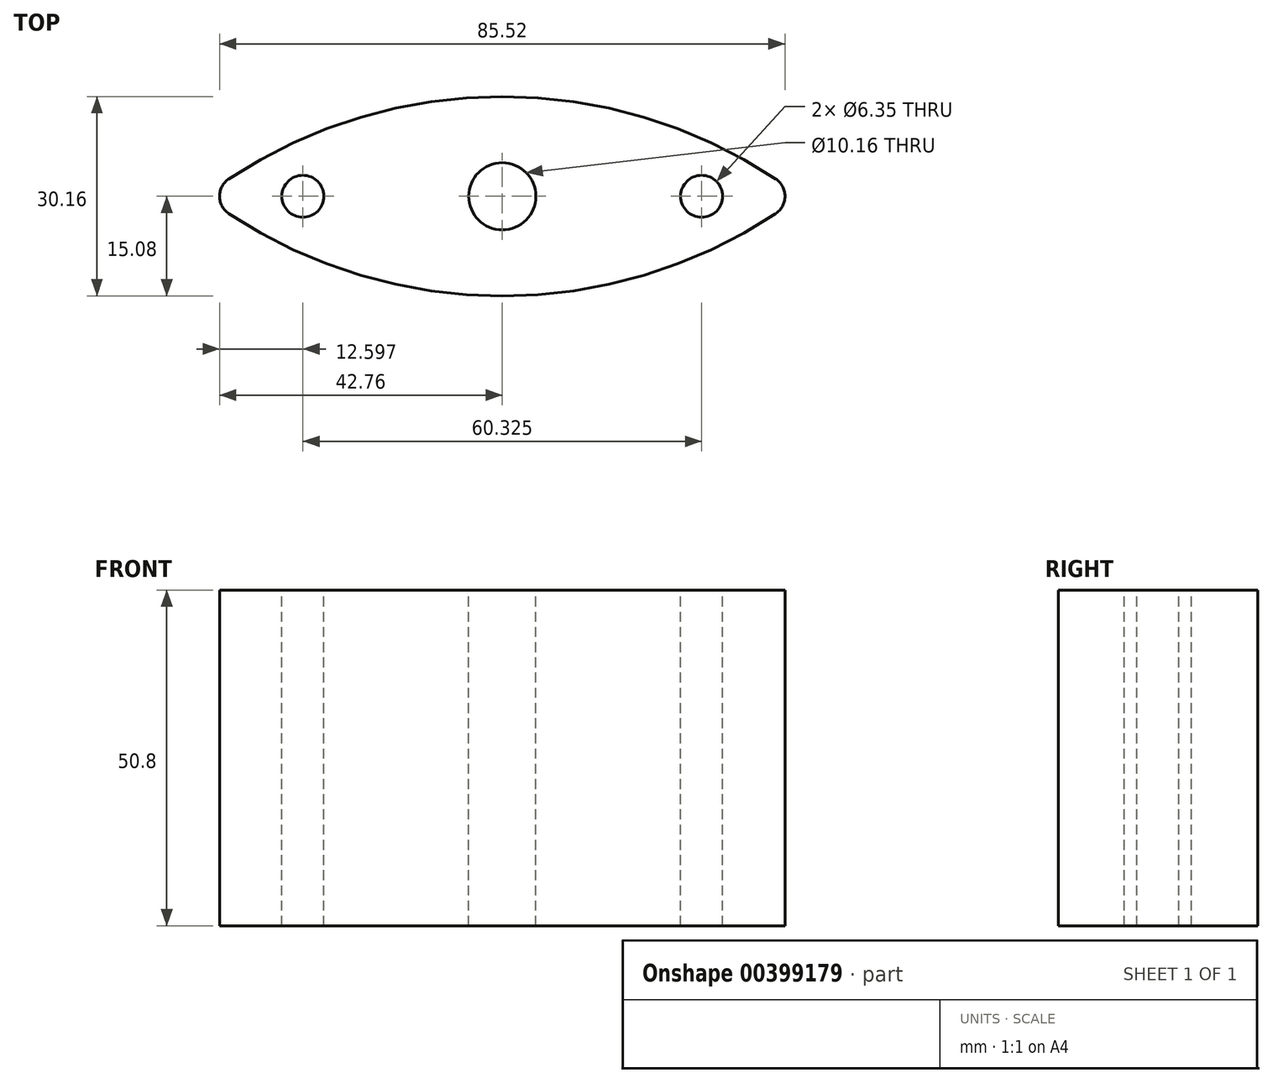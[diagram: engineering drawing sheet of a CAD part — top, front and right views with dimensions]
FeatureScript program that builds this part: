
annotation { "Feature Type Name" : "Feature", "Feature Type Description" : "" }
export const myFeature = defineFeature(function(context is Context, id is Id, definition is map)
    precondition{}
    {
        {
            var Q0;
            Q0=qCreatedBy(makeId("Top.planeOp"),FACE);
            var sketch = newSketch(context, id + "F0", { "sketchPlane" : qUnion([Q0])});
            skArc(sketch, "E0", {"start": v(40.43, 2.7) * mm, "mid": v(0, 14.29) * mm, "end": v(-40.43, 2.7) * mm});
            skArc(sketch, "E1", {"start": v(-40.43, -2.7) * mm, "mid": v(0, -14.29) * mm, "end": v(40.43, -2.7) * mm});
            skArc(sketch, "E2", {"start": v(-40.43, 2.7) * mm, "mid": v(-41.92, 0) * mm, "end": v(-40.43, -2.7) * mm});
            skArc(sketch, "E3", {"start": v(40.43, -2.7) * mm, "mid": v(41.92, 0) * mm, "end": v(40.43, 2.7) * mm});
            skPoint(sketch, "E4.orphan", {"position": v(44.45, 0) * mm});
            skPoint(sketch, "E5.orphan", {"position": v(-44.45, 0) * mm});
            skArc(sketch, "E6", {"start": v(148.38, 2.7) * mm, "mid": v(107.95, 14.29) * mm, "end": v(67.52, 2.7) * mm});
            skArc(sketch, "E7", {"start": v(67.52, -2.7) * mm, "mid": v(107.95, -14.29) * mm, "end": v(148.38, -2.7) * mm});
            skArc(sketch, "E8", {"start": v(67.52, 2.7) * mm, "mid": v(66.03, 0) * mm, "end": v(67.52, -2.7) * mm});
            skArc(sketch, "E9", {"start": v(148.38, -2.7) * mm, "mid": v(149.87, 0) * mm, "end": v(148.38, 2.7) * mm});
            skPoint(sketch, "E10.orphan", {"position": v(152.4, 0) * mm});
            skPoint(sketch, "E11.orphan", {"position": v(63.5, 0) * mm});
            skArc(sketch, "E12", {"start": v(41.34, -48.15) * mm, "mid": v(0, -35.72) * mm, "end": v(-41.34, -48.15) * mm});
            skArc(sketch, "E13", {"start": v(-41.34, -53.45) * mm, "mid": v(0, -65.88) * mm, "end": v(41.34, -53.45) * mm});
            skArc(sketch, "E14", {"start": v(-41.34, -48.15) * mm, "mid": v(-42.76, -50.8) * mm, "end": v(-41.34, -53.45) * mm});
            skArc(sketch, "E15", {"start": v(41.34, -53.45) * mm, "mid": v(42.76, -50.8) * mm, "end": v(41.34, -48.15) * mm});
            skPoint(sketch, "E16.orphan", {"position": v(45.08, -50.8) * mm});
            skPoint(sketch, "E17.orphan", {"position": v(-45.09, -50.8) * mm});
            skArc(sketch, "E18", {"start": v(149.29, -48.15) * mm, "mid": v(107.95, -35.72) * mm, "end": v(66.61, -48.15) * mm});
            skArc(sketch, "E19", {"start": v(66.61, -53.45) * mm, "mid": v(107.95, -65.88) * mm, "end": v(149.29, -53.45) * mm});
            skArc(sketch, "E20", {"start": v(66.61, -48.15) * mm, "mid": v(65.2, -50.8) * mm, "end": v(66.61, -53.45) * mm});
            skArc(sketch, "E21", {"start": v(149.29, -53.45) * mm, "mid": v(150.7, -50.8) * mm, "end": v(149.29, -48.15) * mm});
            skPoint(sketch, "E22.orphan", {"position": v(153.04, -50.8) * mm});
            skPoint(sketch, "E23.orphan", {"position": v(62.87, -50.8) * mm});
            skArc(sketch, "E24", {"start": v(42.21, -99) * mm, "mid": v(0, -85.72) * mm, "end": v(-42.21, -99) * mm});
            skArc(sketch, "E25", {"start": v(-42.21, -104.2) * mm, "mid": v(0, -117.48) * mm, "end": v(42.21, -104.2) * mm});
            skArc(sketch, "E26", {"start": v(-42.21, -99) * mm, "mid": v(-43.57, -101.6) * mm, "end": v(-42.21, -104.2) * mm});
            skArc(sketch, "E27", {"start": v(42.21, -104.2) * mm, "mid": v(43.57, -101.6) * mm, "end": v(42.21, -99) * mm});
            skPoint(sketch, "E28.orphan", {"position": v(45.72, -101.6) * mm});
            skPoint(sketch, "E29.orphan", {"position": v(-45.72, -101.6) * mm});
            skArc(sketch, "E30", {"start": v(150.16, -99) * mm, "mid": v(107.95, -85.72) * mm, "end": v(65.74, -99) * mm});
            skArc(sketch, "E31", {"start": v(65.74, -104.2) * mm, "mid": v(107.95, -117.47) * mm, "end": v(150.16, -104.2) * mm});
            skArc(sketch, "E32", {"start": v(65.74, -99) * mm, "mid": v(64.38, -101.6) * mm, "end": v(65.74, -104.2) * mm});
            skArc(sketch, "E33", {"start": v(150.16, -104.2) * mm, "mid": v(151.52, -101.6) * mm, "end": v(150.16, -99) * mm});
            skPoint(sketch, "E34.orphan", {"position": v(153.67, -101.6) * mm});
            skPoint(sketch, "E35.orphan", {"position": v(62.23, -101.6) * mm});
            skCircle(sketch, "E36", {"center": v(-30.16, 0) * mm, "radius": 3.18 * mm});
            skCircle(sketch, "E37", {"center": v(30.16, 0) * mm, "radius": 3.18 * mm});
            skCircle(sketch, "E38", {"center": v(-30.16, -50.8) * mm, "radius": 3.18 * mm});
            skCircle(sketch, "E39", {"center": v(30.16, -50.8) * mm, "radius": 3.18 * mm});
            skCircle(sketch, "E40", {"center": v(-30.16, -101.6) * mm, "radius": 3.18 * mm});
            skCircle(sketch, "E41", {"center": v(30.16, -101.6) * mm, "radius": 3.18 * mm});
            skCircle(sketch, "E42", {"center": v(77.79, -101.6) * mm, "radius": 3.18 * mm});
            skCircle(sketch, "E43", {"center": v(138.11, -101.6) * mm, "radius": 3.18 * mm});
            skCircle(sketch, "E44", {"center": v(138.11, -50.8) * mm, "radius": 3.18 * mm});
            skCircle(sketch, "E45", {"center": v(77.79, -50.8) * mm, "radius": 3.18 * mm});
            skCircle(sketch, "E46", {"center": v(77.79, 0) * mm, "radius": 3.18 * mm});
            skCircle(sketch, "E47", {"center": v(138.11, 0) * mm, "radius": 3.18 * mm});
            skLineSegment(sketch, "E48", {"start": v(107.95, 9.05) * mm, "end": v(107.95, -43.7) * mm, "construction": true});
            skLineSegment(sketch, "E49", {"start": v(-30.16, 0) * mm, "end": v(30.16, 0) * mm, "construction": true});
            skLineSegment(sketch, "E50", {"start": v(-30.16, -50.8) * mm, "end": v(30.16, -50.8) * mm, "construction": true});
            skLineSegment(sketch, "E51", {"start": v(-30.16, -101.6) * mm, "end": v(30.16, -101.6) * mm, "construction": true});
            skLineSegment(sketch, "E52", {"start": v(77.79, 0) * mm, "end": v(138.11, 0) * mm, "construction": true});
            skLineSegment(sketch, "E53", {"start": v(77.79, -50.8) * mm, "end": v(138.11, -50.8) * mm, "construction": true});
            skLineSegment(sketch, "E54", {"start": v(77.79, -101.6) * mm, "end": v(138.11, -101.6) * mm, "construction": true});
            skCircle(sketch, "E55", {"center": v(0, 0) * mm, "radius": 5.08 * mm});
            skCircle(sketch, "E56", {"center": v(0, -50.8) * mm, "radius": 5.08 * mm});
            skCircle(sketch, "E57", {"center": v(0, -101.6) * mm, "radius": 5.08 * mm});
            skCircle(sketch, "E58", {"center": v(107.95, 0) * mm, "radius": 5.08 * mm});
            skCircle(sketch, "E59", {"center": v(107.95, -50.8) * mm, "radius": 5.08 * mm});
            skCircle(sketch, "E60", {"center": v(107.95, -101.6) * mm, "radius": 5.08 * mm});
            skSolve(sketch);
        }
        {
            var Q0;
            Q0=makeQuery(id+"F0.imprint","IMPRINT",FACE,{"disambiguationData":[TD([[makeQuery(id+"F0.imprint","IMPRINT",EDGE,{"derivedFrom":sQuery(id+"F0.wireOp",EDGE,"E12")}),1.0]])]});
            extrude(context, id + "F1", {"entities" : qUnion([Q0]), "oppositeDirection" : true, "depth" : 50.8 * mm, "offsetDistance" : 25.4 * mm});
        }
    });
